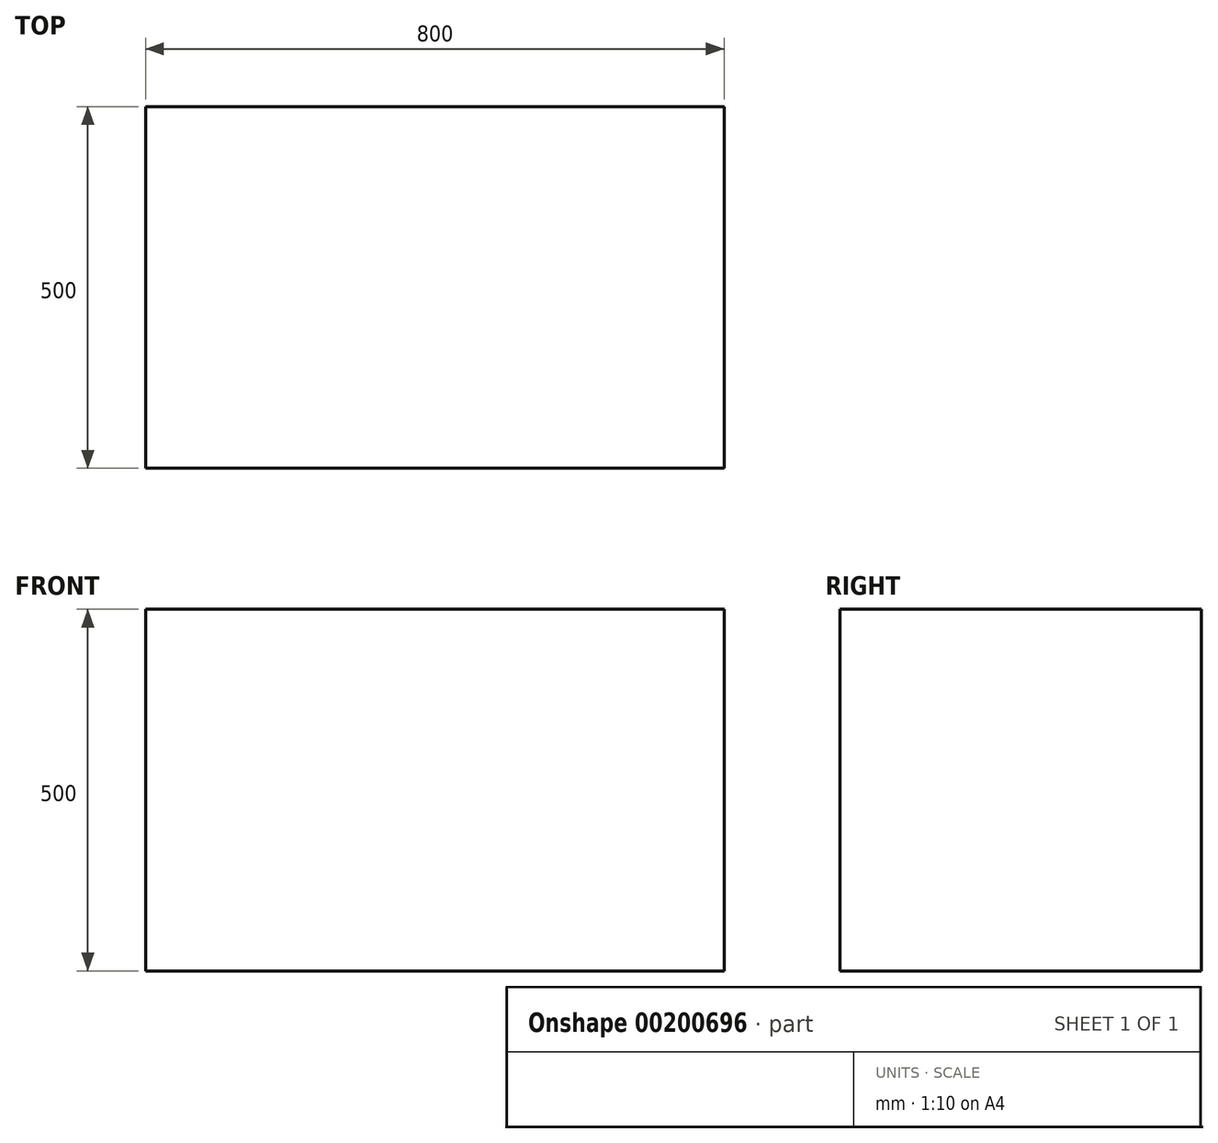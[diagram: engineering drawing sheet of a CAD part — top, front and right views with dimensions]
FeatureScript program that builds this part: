
annotation { "Feature Type Name" : "Feature", "Feature Type Description" : "" }
export const myFeature = defineFeature(function(context is Context, id is Id, definition is map)
    precondition{}
    {
        {
            var Q0;
            Q0=qCreatedBy(makeId("Front.planeOp"),FACE);
            var sketch = newSketch(context, id + "F0", { "sketchPlane" : qUnion([Q0])});
            skLineSegment(sketch, "E0.bottom", {"start": v(0, 0) * mm, "end": v(800, 0) * mm});
            skLineSegment(sketch, "E0.top", {"start": v(0, 500) * mm, "end": v(800, 500) * mm});
            skLineSegment(sketch, "E0.left", {"start": v(0, 0) * mm, "end": v(0, 500) * mm});
            skLineSegment(sketch, "E0.right", {"start": v(800, 0) * mm, "end": v(800, 500) * mm});
            skSolve(sketch);
        }
        {
            var Q0;
            Q0=qSketchRegion(id+"F0",true);
            extrude(context, id + "F1", {"entities" : qUnion([Q0]), "depth" : 500 * mm});
        }
    });
